# Revit family: 304_F382_2__
name_source: partatom
category: Pipe Accessories
revit_build: Autodesk Revit MEP 2016 (Build: 20150714_1515(x64)
units: mm (PartAtom-declared; Revit-internal decimal feet)

## family parameters
Always vertical = Yes
Cut with Voids When Loaded = No
Part Type = Valve - Breaks Into
Round Connector Dimension = Use Diameter
Shared = No
Work Plane-Based = No

## types (2) — shared parameters
A = 60.00°
CenSd_RN_6 = 10 mm  [stored 0.0328084 ft]
Description = K - Automatic Balancing Valve - Accessible Pre-Set Cartridge
H4 = 49 mm
H5 = 73 mm
L2D_Min = 3048 mm  [stored 10 ft]
Manufacturer = FlowCon
QmdConnectorList = 301;D;302;D
R3 = 6 mm  [stored 0.019685 ft]
R4 = 11 mm  [stored 0.0360892 ft]
RN = 12 mm  [stored 0.0393701 ft]
URL = http://flowcon.com
magiPartTypeId = 304
magiProductFamilyId = F382.2.*
zero-valued in all types: MC_Default_elevation

## per-type parameters (varying)
| type | CenSd_SW_6 | D | H6 | L1 | L1__ve | L2 | L2D | L3 | L4 | LL | R | R1 | R2 | SW | W2D | magiProductId |
| F382.2.K.B | 25 mm  [stored 0.082021 ft] | 40 mm | 43 mm | 27 mm | -27 mm | 113 mm | 166 mm | 50 mm  [stored 0.164042 ft] | 38 mm | 83 mm  [stored 0.27231 ft] | 23 mm  [stored 0.0754593 ft] | 23 mm  [stored 0.0754593 ft] | 28 mm  [stored 0.0918635 ft] | 29 mm  [stored 0.0951444 ft] | 40 mm  [stored 0.131234 ft] | F382.2.K |
| F382.2.L.B | 30 mm  [stored 0.0984252 ft] | 50 mm | 44 mm  [stored 0.144357 ft] | 28 mm  [stored 0.0918635 ft] | -28 mm  [stored -0.0918635 ft] | 118 mm | 174 mm | 52 mm | 39 mm | 87 mm  [stored 0.285433 ft] | 26 mm | 28 mm  [stored 0.0918635 ft] | 31 mm | 35 mm  [stored 0.114829 ft] | 50 mm  [stored 0.164042 ft] | F382.2.L |

note: column(s) folded — value = type name in every type: magiProductCode

note: [stored X ft] marks values corroborated as IEEE doubles in the binary element streams (Revit-internal decimal feet)

## geometry (parser evidence)
native form markers: Sweep x2
no freeform markers — native parametric forms only
